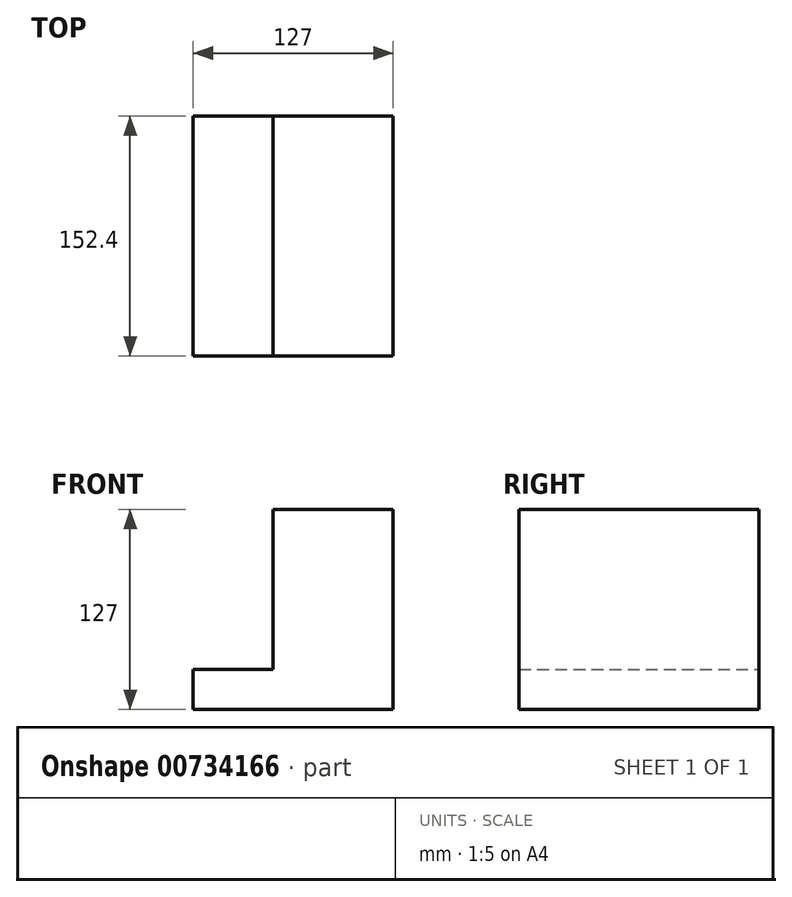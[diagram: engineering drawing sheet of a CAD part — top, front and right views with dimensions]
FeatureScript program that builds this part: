
annotation { "Feature Type Name" : "Feature", "Feature Type Description" : "" }
export const myFeature = defineFeature(function(context is Context, id is Id, definition is map)
    precondition{}
    {
        {
            var Q0;
            Q0=qCreatedBy(makeId("Front.planeOp"),FACE);
            var sketch = newSketch(context, id + "F0", { "sketchPlane" : qUnion([Q0])});
            skLineSegment(sketch, "E0", {"start": v(-60.88, -75.78) * mm, "end": v(66.12, -75.78) * mm});
            skLineSegment(sketch, "E1", {"start": v(-60.88, -75.78) * mm, "end": v(-60.88, -50.38) * mm});
            skLineSegment(sketch, "E2", {"start": v(-60.88, -50.38) * mm, "end": v(-10.08, -50.38) * mm});
            skLineSegment(sketch, "E3", {"start": v(-10.08, -50.38) * mm, "end": v(-10.08, 51.22) * mm});
            skLineSegment(sketch, "E4", {"start": v(-10.08, 51.22) * mm, "end": v(66.12, 51.22) * mm});
            skLineSegment(sketch, "E5", {"start": v(66.12, 51.22) * mm, "end": v(66.12, -75.78) * mm});
            skSolve(sketch);
        }
        {
            var Q0;
            Q0 = qSketchRegion(id + "F0", true);
            extrude(context, id + "F1", {"entities" : qUnion([Q0]), "depth" : 152.4 * mm, "offsetDistance" : 25.4 * mm});
        }
    });
